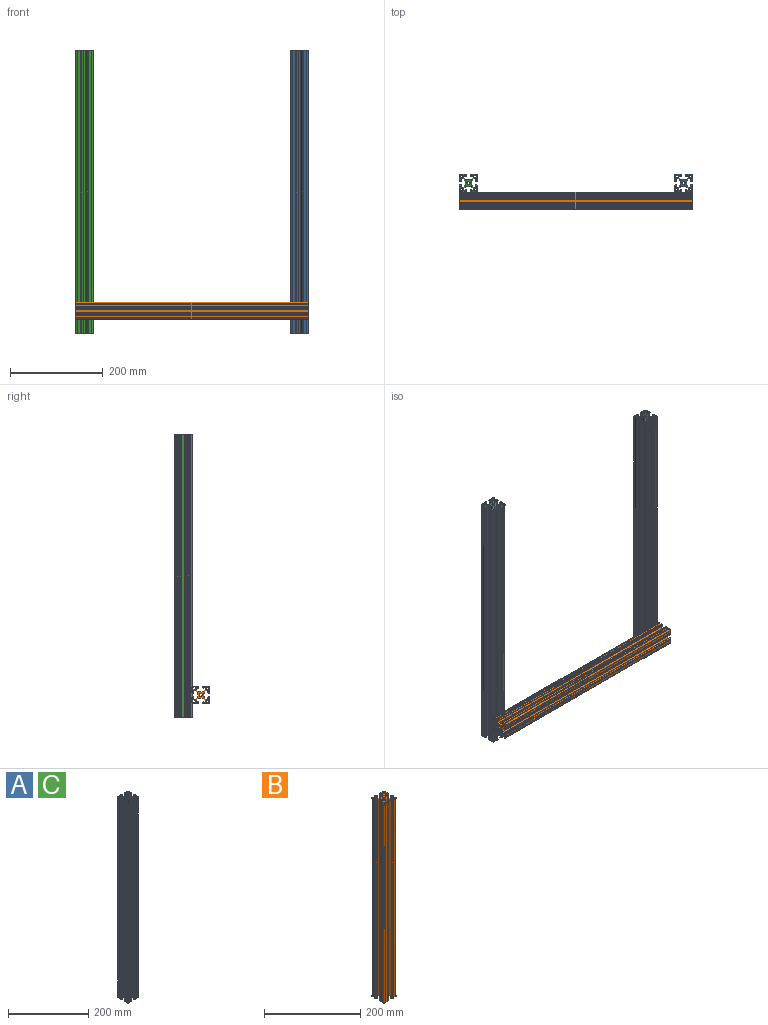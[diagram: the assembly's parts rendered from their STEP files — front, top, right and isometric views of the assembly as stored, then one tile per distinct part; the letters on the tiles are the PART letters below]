
ASSEMBLY  parts=3 mates=5
PART A: 171 faces, bbox 38.1x38.1x609.6 mm
  f0: cylinder r=4.75mm len=609.6mm, axis (0,0,-1), area 2273.9mm2, adj f1,f168,f169,f170
  f1: plane 609.6x4.01mm, normal (0.71,0.71,0), area 3452.7mm2, adj f0,f2,f169,f170
  f2: cylinder r=0.89mm len=609.6mm, axis (0,0,-1), area 425.5mm2, adj f1,f3,f169,f170
  f3: plane 609.6x1.77mm, normal (1,0,0), area 1081.7mm2, adj f2,f4,f169,f170
  f4: cylinder r=1.27mm len=609.6mm, axis (0,0,-1), area 1216.1mm2, adj f3,f5,f169,f170
  f5: plane 609.6x2.2mm, normal (0,-1,0), area 1342.9mm2, adj f4,f6,f169,f170
  f6: plane 609.6x0.84mm, normal (-1,0,0), area 511.3mm2, adj f5,f7,f169,f170
  f7: plane 609.6x1.18mm, normal (0,-1,0), area 716.5mm2, adj f6,f8,f169,f170
  f8: cylinder r=1.57mm len=609.6mm, axis (0,0,-1), area 1508mm2, adj f7,f9,f169,f170
  f9: plane 609.6x0.91mm, normal (1,0,0), area 557.4mm2, adj f8,f10,f169,f170
  f10: cylinder r=1.57mm len=609.6mm, axis (0,0,-1), area 1508mm2, adj f9,f11,f169,f170
  f11: plane 609.6x2.34mm, normal (0,1,0), area 1424.5mm2, adj f10,f12,f169,f170
  f12: cylinder r=0.76mm len=609.6mm, axis (0,0,-1), area 1459.3mm2, adj f11,f13,f169,f170
  f13: plane 609.6x4.83mm, normal (0,1,0), area 2941.9mm2, adj f12,f14,f169,f170
  f14: cylinder r=0.76mm len=609.6mm, axis (0,0,-1), area 1459.3mm2, adj f13,f15,f169,f170
  f15: plane 609.6x0.03mm, normal (0,1,0), area 15.5mm2, adj f14,f16,f169,f170
  f16: cylinder r=3.17mm len=609.6mm, axis (0,0,-1), area 3040.2mm2, adj f15,f17,f169,f170
  f17: plane 609.6x0.03mm, normal (-1,0,0), area 15.5mm2, adj f16,f18,f169,f170
  f18: cylinder r=0.76mm len=609.6mm, axis (0,0,-1), area 1459.3mm2, adj f17,f19,f169,f170
  f19: plane 609.6x4.83mm, normal (-1,0,0), area 2941.9mm2, adj f18,f20,f169,f170
  f20: cylinder r=0.76mm len=609.6mm, axis (0,0,-1), area 1459.3mm2, adj f19,f21,f169,f170
  f21: plane 609.6x2.34mm, normal (-1,0,0), area 1424.5mm2, adj f20,f22,f169,f170
  f22: cylinder r=1.57mm len=609.6mm, axis (0,0,-1), area 1508mm2, adj f21,f23,f169,f170
  f23: plane 609.6x0.91mm, normal (0,-1,0), area 557.4mm2, adj f22,f24,f169,f170
  f24: cylinder r=1.57mm len=609.6mm, axis (0,0,-1), area 1508mm2, adj f23,f25,f169,f170
  f25: plane 609.6x1.11mm, normal (1,0,0), area 677.8mm2, adj f24,f26,f169,f170
  f26: plane 609.6x0.89mm, normal (0,1,0), area 544.4mm2, adj f25,f27,f169,f170
  f27: plane 609.6x2.17mm, normal (1,0,0), area 1322mm2, adj f26,f28,f169,f170
  f28: cylinder r=1.27mm len=609.6mm, axis (0,0,-1), area 1216.1mm2, adj f27,f29,f169,f170
  f29: plane 609.6x1.87mm, normal (0,-1,0), area 1137.7mm2, adj f28,f30,f169,f170
  f30: cylinder r=0.89mm len=609.6mm, axis (0,0,-1), area 425.6mm2, adj f29,f31,f169,f170
  f31: plane 609.6x3.97mm, normal (-0.71,-0.71,0), area 3419.1mm2, adj f30,f32,f169,f170
  f32: cylinder r=4.75mm len=609.6mm, axis (0,0,-1), area 2274.3mm2, adj f31,f33,f169,f170
  f33: plane 609.6x5.21mm, normal (-1,0,0), area 3175.2mm2, adj f32,f34,f169,f170
  f34: cylinder r=4.75mm len=609.6mm, axis (0,0,-1), area 2274.3mm2, adj f33,f35,f169,f170
  f35: plane 609.6x3.97mm, normal (-0.71,0.71,0), area 3419.1mm2, adj f34,f36,f169,f170
  f36: cylinder r=0.89mm len=609.6mm, axis (0,0,-1), area 425.6mm2, adj f35,f37,f169,f170
  f37: plane 609.6x1.87mm, normal (0,1,0), area 1137.7mm2, adj f36,f38,f169,f170
  f38: cylinder r=1.27mm len=609.6mm, axis (0,0,-1), area 1216.1mm2, adj f37,f39,f169,f170
  f39: plane 609.6x2.17mm, normal (1,0,0), area 1322mm2, adj f38,f40,f169,f170
  f40: plane 609.6x0.89mm, normal (0,-1,0), area 544.4mm2, adj f39,f41,f169,f170
  f41: plane 609.6x1.11mm, normal (1,0,0), area 677.8mm2, adj f40,f42,f169,f170
  f42: cylinder r=1.57mm len=609.6mm, axis (0,0,-1), area 1508mm2, adj f41,f43,f169,f170
  f43: plane 609.6x0.91mm, normal (0,1,0), area 557.4mm2, adj f42,f44,f169,f170
  f44: cylinder r=1.57mm len=609.6mm, axis (0,0,-1), area 1508mm2, adj f43,f45,f169,f170
  f45: plane 609.6x2.34mm, normal (-1,0,0), area 1424.5mm2, adj f44,f46,f169,f170
  f46: cylinder r=0.76mm len=609.6mm, axis (0,0,-1), area 1459.3mm2, adj f45,f47,f169,f170
  f47: plane 609.6x4.83mm, normal (-1,0,0), area 2941.9mm2, adj f46,f48,f169,f170
  f48: cylinder r=0.76mm len=609.6mm, axis (0,0,-1), area 1459.3mm2, adj f47,f49,f169,f170
  f49: plane 609.6x0.03mm, normal (-1,0,0), area 15.5mm2, adj f48,f50,f169,f170
  f50: cylinder r=3.17mm len=609.6mm, axis (0,0,-1), area 3040.2mm2, adj f49,f51,f169,f170
  f51: plane 609.6x0.03mm, normal (0,-1,0), area 15.5mm2, adj f50,f52,f169,f170
  f52: cylinder r=0.76mm len=609.6mm, axis (0,0,-1), area 1459.3mm2, adj f51,f53,f169,f170
  f53: plane 609.6x4.83mm, normal (0,-1,0), area 2941.9mm2, adj f52,f54,f169,f170
  f54: cylinder r=0.76mm len=609.6mm, axis (0,0,-1), area 1459.3mm2, adj f53,f55,f169,f170
  f55: plane 609.6x2.34mm, normal (0,-1,0), area 1424.5mm2, adj f54,f56,f169,f170
  f56: cylinder r=1.57mm len=609.6mm, axis (0,0,-1), area 1508mm2, adj f55,f57,f169,f170
  f57: plane 609.6x0.91mm, normal (1,0,0), area 557.4mm2, adj f56,f58,f169,f170
  f58: cylinder r=1.57mm len=609.6mm, axis (0,0,-1), area 1508mm2, adj f57,f59,f169,f170
  f59: plane 609.6x1.18mm, normal (0,1,0), area 716.5mm2, adj f58,f60,f169,f170
  f60: plane 609.6x0.84mm, normal (-1,0,0), area 511.3mm2, adj f59,f61,f169,f170
  f61: plane 609.6x2.2mm, normal (0,1,0), area 1342.9mm2, adj f60,f62,f169,f170
  f62: cylinder r=1.27mm len=609.6mm, axis (0,0,-1), area 1216.1mm2, adj f61,f63,f169,f170
  f63: plane 609.6x1.77mm, normal (1,0,0), area 1081.7mm2, adj f62,f64,f169,f170
  f64: cylinder r=0.89mm len=609.6mm, axis (0,0,-1), area 425.5mm2, adj f63,f65,f169,f170
  f65: plane 609.6x4.01mm, normal (0.71,-0.71,0), area 3452.7mm2, adj f64,f66,f169,f170
  f66: cylinder r=4.75mm len=609.6mm, axis (0,0,-1), area 2273.9mm2, adj f65,f67,f169,f170
  f67: plane 609.6x5.33mm, normal (0,-1,0), area 3246.9mm2, adj f66,f68,f169,f170
  f68: cylinder r=4.75mm len=609.6mm, axis (0,0,-1), area 2273.9mm2, adj f67,f69,f169,f170
  f69: plane 609.6x4.01mm, normal (-0.71,-0.71,0), area 3452.7mm2, adj f68,f70,f169,f170
  f70: cylinder r=0.89mm len=609.6mm, axis (0,0,-1), area 425.5mm2, adj f69,f71,f169,f170
  f71: plane 609.6x1.77mm, normal (-1,0,0), area 1081.7mm2, adj f70,f72,f169,f170
  f72: cylinder r=1.27mm len=609.6mm, axis (0,0,-1), area 1216.1mm2, adj f71,f73,f169,f170
  f73: plane 609.6x2.2mm, normal (0,1,0), area 1342.9mm2, adj f72,f74,f169,f170
  f74: plane 609.6x0.84mm, normal (1,0,0), area 511.3mm2, adj f73,f75,f169,f170
  f75: plane 609.6x1.18mm, normal (0,1,0), area 716.5mm2, adj f74,f76,f169,f170
  f76: cylinder r=1.57mm len=609.6mm, axis (0,0,-1), area 1508mm2, adj f75,f77,f169,f170
  f77: plane 609.6x0.91mm, normal (-1,0,0), area 557.4mm2, adj f76,f78,f169,f170
  f78: cylinder r=1.57mm len=609.6mm, axis (0,0,-1), area 1508mm2, adj f77,f79,f169,f170
  f79: plane 609.6x2.34mm, normal (0,-1,0), area 1424.5mm2, adj f78,f80,f169,f170
  f80: cylinder r=0.76mm len=609.6mm, axis (0,0,-1), area 1459.3mm2, adj f79,f81,f169,f170
  f81: plane 609.6x4.83mm, normal (0,-1,0), area 2941.9mm2, adj f80,f82,f169,f170
  f82: cylinder r=0.76mm len=609.6mm, axis (0,0,-1), area 1459.3mm2, adj f81,f83,f169,f170
  f83: plane 609.6x0.03mm, normal (0,-1,0), area 15.5mm2, adj f82,f84,f169,f170
  f84: cylinder r=3.17mm len=609.6mm, axis (0,0,-1), area 3040.2mm2, adj f83,f85,f169,f170
  f85: plane 609.6x0.03mm, normal (1,0,0), area 15.5mm2, adj f84,f86,f169,f170
  f86: cylinder r=0.76mm len=609.6mm, axis (0,0,-1), area 1459.3mm2, adj f85,f87,f169,f170
  f87: plane 609.6x4.83mm, normal (1,0,0), area 2941.9mm2, adj f86,f88,f169,f170
  f88: cylinder r=0.76mm len=609.6mm, axis (0,0,-1), area 1459.3mm2, adj f87,f89,f169,f170
  f89: plane 609.6x2.34mm, normal (1,0,0), area 1424.5mm2, adj f88,f90,f169,f170
  f90: cylinder r=1.57mm len=609.6mm, axis (0,0,-1), area 1508mm2, adj f89,f91,f169,f170
  f91: plane 609.6x0.91mm, normal (0,1,0), area 557.4mm2, adj f90,f92,f169,f170
  f92: cylinder r=1.57mm len=609.6mm, axis (0,0,-1), area 1508mm2, adj f91,f93,f169,f170
  f93: plane 609.6x1.11mm, normal (-1,0,0), area 677.8mm2, adj f92,f94,f169,f170
  f94: plane 609.6x0.89mm, normal (0,-1,0), area 544.4mm2, adj f93,f95,f169,f170
  f95: plane 609.6x2.17mm, normal (-1,0,0), area 1322mm2, adj f94,f96,f169,f170
  f96: cylinder r=1.27mm len=609.6mm, axis (0,0,-1), area 1216.1mm2, adj f95,f97,f169,f170
  f97: plane 609.6x1.87mm, normal (0,1,0), area 1137.7mm2, adj f96,f98,f169,f170
  f98: cylinder r=0.89mm len=609.6mm, axis (0,0,-1), area 425.6mm2, adj f97,f99,f169,f170
  f99: plane 609.6x3.97mm, normal (0.71,0.71,0), area 3419.1mm2, adj f98,f100,f169,f170
  f100: cylinder r=4.75mm len=609.6mm, axis (0,0,-1), area 2274.3mm2, adj f99,f101,f169,f170
  f101: plane 609.6x5.21mm, normal (1,0,0), area 3175.2mm2, adj f100,f102,f169,f170
  f102: cylinder r=4.75mm len=609.6mm, axis (0,0,-1), area 2274.3mm2, adj f101,f103,f169,f170
  f103: plane 609.6x3.97mm, normal (0.71,-0.71,0), area 3419.1mm2, adj f102,f104,f169,f170
  f104: cylinder r=0.89mm len=609.6mm, axis (0,0,-1), area 425.6mm2, adj f103,f105,f169,f170
  f105: plane 609.6x1.87mm, normal (0,-1,0), area 1137.7mm2, adj f104,f106,f169,f170
  f106: cylinder r=1.27mm len=609.6mm, axis (0,0,-1), area 1216.1mm2, adj f105,f107,f169,f170
  f107: plane 609.6x2.17mm, normal (-1,0,0), area 1322mm2, adj f106,f108,f169,f170
  f108: plane 609.6x0.89mm, normal (0,1,0), area 544.4mm2, adj f107,f109,f169,f170
  f109: plane 609.6x1.11mm, normal (-1,0,0), area 677.8mm2, adj f108,f110,f169,f170
  f110: cylinder r=1.57mm len=609.6mm, axis (0,0,-1), area 1508mm2, adj f109,f111,f169,f170
  f111: plane 609.6x0.91mm, normal (0,-1,0), area 557.4mm2, adj f110,f112,f169,f170
  f112: cylinder r=1.57mm len=609.6mm, axis (0,0,-1), area 1508mm2, adj f111,f113,f169,f170
  f113: plane 609.6x2.34mm, normal (1,0,0), area 1424.5mm2, adj f112,f114,f169,f170
  f114: cylinder r=0.76mm len=609.6mm, axis (0,0,-1), area 1459.3mm2, adj f113,f115,f169,f170
  f115: plane 609.6x4.83mm, normal (1,0,0), area 2941.9mm2, adj f114,f116,f169,f170
  f116: cylinder r=0.76mm len=609.6mm, axis (0,0,-1), area 1459.3mm2, adj f115,f117,f169,f170
  f117: plane 609.6x0.03mm, normal (1,0,0), area 15.5mm2, adj f116,f118,f169,f170
  f118: cylinder r=3.17mm len=609.6mm, axis (0,0,-1), area 3040.2mm2, adj f117,f119,f169,f170
  f119: plane 609.6x0.03mm, normal (0,1,0), area 15.5mm2, adj f118,f120,f169,f170
  f120: cylinder r=0.76mm len=609.6mm, axis (0,0,-1), area 1459.3mm2, adj f119,f121,f169,f170
  f121: plane 609.6x4.83mm, normal (0,1,0), area 2941.9mm2, adj f120,f122,f169,f170
  f122: cylinder r=0.76mm len=609.6mm, axis (0,0,-1), area 1459.3mm2, adj f121,f123,f169,f170
  f123: plane 609.6x2.34mm, normal (0,1,0), area 1424.5mm2, adj f122,f124,f169,f170
  f124: cylinder r=1.57mm len=609.6mm, axis (0,0,-1), area 1508mm2, adj f123,f125,f169,f170
  f125: plane 609.6x0.91mm, normal (-1,0,0), area 557.4mm2, adj f124,f126,f169,f170
  f126: cylinder r=1.57mm len=609.6mm, axis (0,0,-1), area 1508mm2, adj f125,f127,f169,f170
  f127: plane 609.6x1.18mm, normal (0,-1,0), area 716.5mm2, adj f126,f128,f169,f170
  f128: plane 609.6x0.84mm, normal (1,0,0), area 511.3mm2, adj f127,f129,f169,f170
  f129: plane 609.6x2.2mm, normal (0,-1,0), area 1342.9mm2, adj f128,f130,f169,f170
  f130: cylinder r=1.27mm len=609.6mm, axis (0,0,-1), area 1216.1mm2, adj f129,f131,f169,f170
  f131: plane 609.6x1.77mm, normal (-1,0,0), area 1081.7mm2, adj f130,f132,f169,f170
  f132: cylinder r=0.89mm len=609.6mm, axis (0,0,-1), area 425.5mm2, adj f131,f133,f169,f170
  f133: plane 609.6x4.01mm, normal (-0.71,0.71,0), area 3452.7mm2, adj f132,f134,f169,f170
  f134: cylinder r=4.75mm len=609.6mm, axis (0,0,-1), area 2273.9mm2, adj f133,f168,f169,f170
  f135: cylinder r=0.38mm len=609.6mm, axis (0,0,-1), area 364.8mm2, adj f136,f163,f169,f170
  f136: plane 609.6x2.24mm, normal (1,0,0), area 1362.6mm2, adj f135,f137,f169,f170
  f137: cylinder r=2.79mm len=609.6mm, axis (0,0,-1), area 2675.4mm2, adj f136,f138,f169,f170
  f138: plane 609.6x2.24mm, normal (0,-1,0), area 1362.6mm2, adj f137,f139,f169,f170
  f139: cylinder r=0.38mm len=609.6mm, axis (0,0,-1), area 364.8mm2, adj f138,f140,f169,f170
  f140: plane 609.6x4.65mm, normal (-1,0,0), area 2833.5mm2, adj f139,f141,f169,f170
  f141: cylinder r=0.38mm len=609.6mm, axis (0,0,-1), area 364.8mm2, adj f140,f163,f169,f170
  f142: cylinder r=0.38mm len=609.6mm, axis (0,0,-1), area 364.8mm2, adj f143,f164,f169,f170
  f143: plane 609.6x4.65mm, normal (0,1,0), area 2833.5mm2, adj f142,f144,f169,f170
  f144: cylinder r=0.38mm len=609.6mm, axis (0,0,-1), area 364.8mm2, adj f143,f145,f169,f170
  f145: plane 609.6x4.65mm, normal (1,0,0), area 2833.5mm2, adj f144,f146,f169,f170
  f146: cylinder r=0.38mm len=609.6mm, axis (0,0,-1), area 364.8mm2, adj f145,f147,f169,f170
  f147: plane 609.6x2.24mm, normal (0,-1,0), area 1362.6mm2, adj f146,f148,f169,f170
  f148: cylinder r=2.79mm len=609.6mm, axis (0,0,-1), area 2675.4mm2, adj f147,f164,f169,f170
  f149: plane 609.6x2.24mm, normal (-1,0,0), area 1362.6mm2, adj f150,f165,f169,f170
  f150: cylinder r=2.79mm len=609.6mm, axis (0,0,-1), area 2675.4mm2, adj f149,f151,f169,f170
  f151: plane 609.6x2.24mm, normal (0,1,0), area 1362.6mm2, adj f150,f152,f169,f170
  f152: cylinder r=0.38mm len=609.6mm, axis (0,0,-1), area 364.8mm2, adj f151,f153,f169,f170
  f153: plane 609.6x4.65mm, normal (1,0,0), area 2833.5mm2, adj f152,f154,f169,f170
  f154: cylinder r=0.38mm len=609.6mm, axis (0,0,-1), area 364.8mm2, adj f153,f155,f169,f170
  f155: plane 609.6x4.65mm, normal (0,-1,0), area 2833.5mm2, adj f154,f165,f169,f170
  f156: plane 609.6x4.65mm, normal (-1,0,0), area 2833.5mm2, adj f157,f166,f169,f170
  f157: cylinder r=0.38mm len=609.6mm, axis (0,0,-1), area 364.8mm2, adj f156,f158,f169,f170
  f158: plane 609.6x2.24mm, normal (0,1,0), area 1362.6mm2, adj f157,f159,f169,f170
  f159: cylinder r=2.79mm len=609.6mm, axis (0,0,-1), area 2675.4mm2, adj f158,f160,f169,f170
  f160: plane 609.6x2.24mm, normal (1,0,0), area 1362.6mm2, adj f159,f161,f169,f170
  f161: cylinder r=0.38mm len=609.6mm, axis (0,0,-1), area 364.8mm2, adj f160,f162,f169,f170
  f162: plane 609.6x4.65mm, normal (0,-1,0), area 2833.5mm2, adj f161,f166,f169,f170
  f163: plane 609.6x4.65mm, normal (0,1,0), area 2833.5mm2, adj f135,f141,f169,f170
  f164: plane 609.6x2.24mm, normal (-1,0,0), area 1362.6mm2, adj f142,f148,f169,f170
  f165: cylinder r=0.38mm len=609.6mm, axis (0,0,-1), area 364.8mm2, adj f149,f155,f169,f170
  f166: cylinder r=0.38mm len=609.6mm, axis (0,0,-1), area 364.8mm2, adj f156,f162,f169,f170
  f167: cylinder r=3.33mm len=609.6mm, axis (0,0,-1), area 12744.7mm2, adj f169,f170
  f168: plane 609.6x5.33mm, normal (0,1,0), area 3246.9mm2, adj f0,f134,f169,f170
  f169: plane 38.1x38.1mm, normal (0,0,1), area 578.8mm2, adj f0,f1,f2,f3,f4,f5,f6,f7
  f170: plane 38.1x38.1mm, normal (0,0,-1), area 578.8mm2, adj f0,f1,f2,f3,f4,f5,f6,f7
PART B: 171 faces, bbox 38.1x38.1x502.4 mm
  f0: cylinder r=4.75mm len=502.41mm, axis (0,0,-1), area 1874mm2, adj f1,f168,f169,f170
  f1: plane 502.41x4.01mm, normal (0.71,0.71,0), area 2845.6mm2, adj f0,f2,f169,f170
  f2: cylinder r=0.89mm len=502.41mm, axis (0,0,-1), area 350.6mm2, adj f1,f3,f169,f170
  f3: plane 502.41x1.77mm, normal (1,0,0), area 891.5mm2, adj f2,f4,f169,f170
  f4: cylinder r=1.27mm len=502.41mm, axis (0,0,-1), area 1002.3mm2, adj f3,f5,f169,f170
  f5: plane 502.41x2.2mm, normal (0,-1,0), area 1106.7mm2, adj f4,f6,f169,f170
  f6: plane 502.41x0.84mm, normal (-1,0,0), area 421.4mm2, adj f5,f7,f169,f170
  f7: plane 502.41x1.18mm, normal (0,-1,0), area 590.5mm2, adj f6,f8,f169,f170
  f8: cylinder r=1.57mm len=502.41mm, axis (0,0,-1), area 1242.8mm2, adj f7,f9,f169,f170
  f9: plane 502.41x0.91mm, normal (1,0,0), area 459.4mm2, adj f8,f10,f169,f170
  f10: cylinder r=1.57mm len=502.41mm, axis (0,0,-1), area 1242.8mm2, adj f9,f11,f169,f170
  f11: plane 502.41x2.34mm, normal (0,1,0), area 1174mm2, adj f10,f12,f169,f170
  f12: cylinder r=0.76mm len=502.41mm, axis (0,0,-1), area 1202.7mm2, adj f11,f13,f169,f170
  f13: plane 502.41x4.83mm, normal (0,1,0), area 2424.6mm2, adj f12,f14,f169,f170
  f14: cylinder r=0.76mm len=502.41mm, axis (0,0,-1), area 1202.7mm2, adj f13,f15,f169,f170
  f15: plane 502.41x0.03mm, normal (0,1,0), area 12.8mm2, adj f14,f16,f169,f170
  f16: cylinder r=3.17mm len=502.41mm, axis (0,0,-1), area 2505.7mm2, adj f15,f17,f169,f170
  f17: plane 502.41x0.03mm, normal (-1,0,0), area 12.8mm2, adj f16,f18,f169,f170
  f18: cylinder r=0.76mm len=502.41mm, axis (0,0,-1), area 1202.7mm2, adj f17,f19,f169,f170
  f19: plane 502.41x4.83mm, normal (-1,0,0), area 2424.6mm2, adj f18,f20,f169,f170
  f20: cylinder r=0.76mm len=502.41mm, axis (0,0,-1), area 1202.7mm2, adj f19,f21,f169,f170
  f21: plane 502.41x2.34mm, normal (-1,0,0), area 1174mm2, adj f20,f22,f169,f170
  f22: cylinder r=1.57mm len=502.41mm, axis (0,0,-1), area 1242.8mm2, adj f21,f23,f169,f170
  f23: plane 502.41x0.91mm, normal (0,-1,0), area 459.4mm2, adj f22,f24,f169,f170
  f24: cylinder r=1.57mm len=502.41mm, axis (0,0,-1), area 1242.8mm2, adj f23,f25,f169,f170
  f25: plane 502.41x1.11mm, normal (1,0,0), area 558.6mm2, adj f24,f26,f169,f170
  f26: plane 502.41x0.89mm, normal (0,1,0), area 448.7mm2, adj f25,f27,f169,f170
  f27: plane 502.41x2.17mm, normal (1,0,0), area 1089.5mm2, adj f26,f28,f169,f170
  f28: cylinder r=1.27mm len=502.41mm, axis (0,0,-1), area 1002.3mm2, adj f27,f29,f169,f170
  f29: plane 502.41x1.87mm, normal (0,-1,0), area 937.6mm2, adj f28,f30,f169,f170
  f30: cylinder r=0.89mm len=502.41mm, axis (0,0,-1), area 350.8mm2, adj f29,f31,f169,f170
  f31: plane 502.41x3.97mm, normal (-0.71,-0.71,0), area 2817.9mm2, adj f30,f32,f169,f170
  f32: cylinder r=4.75mm len=502.41mm, axis (0,0,-1), area 1874.4mm2, adj f31,f33,f169,f170
  f33: plane 502.41x5.21mm, normal (-1,0,0), area 2616.9mm2, adj f32,f34,f169,f170
  f34: cylinder r=4.75mm len=502.41mm, axis (0,0,-1), area 1874.4mm2, adj f33,f35,f169,f170
  f35: plane 502.41x3.97mm, normal (-0.71,0.71,0), area 2817.9mm2, adj f34,f36,f169,f170
  f36: cylinder r=0.89mm len=502.41mm, axis (0,0,-1), area 350.8mm2, adj f35,f37,f169,f170
  f37: plane 502.41x1.87mm, normal (0,1,0), area 937.6mm2, adj f36,f38,f169,f170
  f38: cylinder r=1.27mm len=502.41mm, axis (0,0,-1), area 1002.3mm2, adj f37,f39,f169,f170
  f39: plane 502.41x2.17mm, normal (1,0,0), area 1089.5mm2, adj f38,f40,f169,f170
  f40: plane 502.41x0.89mm, normal (0,-1,0), area 448.7mm2, adj f39,f41,f169,f170
  f41: plane 502.41x1.11mm, normal (1,0,0), area 558.6mm2, adj f40,f42,f169,f170
  f42: cylinder r=1.57mm len=502.41mm, axis (0,0,-1), area 1242.8mm2, adj f41,f43,f169,f170
  f43: plane 502.41x0.91mm, normal (0,1,0), area 459.4mm2, adj f42,f44,f169,f170
  f44: cylinder r=1.57mm len=502.41mm, axis (0,0,-1), area 1242.8mm2, adj f43,f45,f169,f170
  f45: plane 502.41x2.34mm, normal (-1,0,0), area 1174mm2, adj f44,f46,f169,f170
  f46: cylinder r=0.76mm len=502.41mm, axis (0,0,-1), area 1202.7mm2, adj f45,f47,f169,f170
  f47: plane 502.41x4.83mm, normal (-1,0,0), area 2424.6mm2, adj f46,f48,f169,f170
  f48: cylinder r=0.76mm len=502.41mm, axis (0,0,-1), area 1202.7mm2, adj f47,f49,f169,f170
  f49: plane 502.41x0.03mm, normal (-1,0,0), area 12.8mm2, adj f48,f50,f169,f170
  f50: cylinder r=3.17mm len=502.41mm, axis (0,0,-1), area 2505.7mm2, adj f49,f51,f169,f170
  f51: plane 502.41x0.03mm, normal (0,-1,0), area 12.8mm2, adj f50,f52,f169,f170
  f52: cylinder r=0.76mm len=502.41mm, axis (0,0,-1), area 1202.7mm2, adj f51,f53,f169,f170
  f53: plane 502.41x4.83mm, normal (0,-1,0), area 2424.6mm2, adj f52,f54,f169,f170
  f54: cylinder r=0.76mm len=502.41mm, axis (0,0,-1), area 1202.7mm2, adj f53,f55,f169,f170
  f55: plane 502.41x2.34mm, normal (0,-1,0), area 1174mm2, adj f54,f56,f169,f170
  f56: cylinder r=1.57mm len=502.41mm, axis (0,0,-1), area 1242.8mm2, adj f55,f57,f169,f170
  f57: plane 502.41x0.91mm, normal (1,0,0), area 459.4mm2, adj f56,f58,f169,f170
  f58: cylinder r=1.57mm len=502.41mm, axis (0,0,-1), area 1242.8mm2, adj f57,f59,f169,f170
  f59: plane 502.41x1.18mm, normal (0,1,0), area 590.5mm2, adj f58,f60,f169,f170
  f60: plane 502.41x0.84mm, normal (-1,0,0), area 421.4mm2, adj f59,f61,f169,f170
  f61: plane 502.41x2.2mm, normal (0,1,0), area 1106.7mm2, adj f60,f62,f169,f170
  f62: cylinder r=1.27mm len=502.41mm, axis (0,0,-1), area 1002.3mm2, adj f61,f63,f169,f170
  f63: plane 502.41x1.77mm, normal (1,0,0), area 891.5mm2, adj f62,f64,f169,f170
  f64: cylinder r=0.89mm len=502.41mm, axis (0,0,-1), area 350.6mm2, adj f63,f65,f169,f170
  f65: plane 502.41x4.01mm, normal (0.71,-0.71,0), area 2845.6mm2, adj f64,f66,f169,f170
  f66: cylinder r=4.75mm len=502.41mm, axis (0,0,-1), area 1874mm2, adj f65,f67,f169,f170
  f67: plane 502.41x5.33mm, normal (0,-1,0), area 2676mm2, adj f66,f68,f169,f170
  f68: cylinder r=4.75mm len=502.41mm, axis (0,0,-1), area 1874mm2, adj f67,f69,f169,f170
  f69: plane 502.41x4.01mm, normal (-0.71,-0.71,0), area 2845.6mm2, adj f68,f70,f169,f170
  f70: cylinder r=0.89mm len=502.41mm, axis (0,0,-1), area 350.6mm2, adj f69,f71,f169,f170
  f71: plane 502.41x1.77mm, normal (-1,0,0), area 891.5mm2, adj f70,f72,f169,f170
  f72: cylinder r=1.27mm len=502.41mm, axis (0,0,-1), area 1002.3mm2, adj f71,f73,f169,f170
  f73: plane 502.41x2.2mm, normal (0,1,0), area 1106.7mm2, adj f72,f74,f169,f170
  f74: plane 502.41x0.84mm, normal (1,0,0), area 421.4mm2, adj f73,f75,f169,f170
  f75: plane 502.41x1.18mm, normal (0,1,0), area 590.5mm2, adj f74,f76,f169,f170
  f76: cylinder r=1.57mm len=502.41mm, axis (0,0,-1), area 1242.8mm2, adj f75,f77,f169,f170
  f77: plane 502.41x0.91mm, normal (-1,0,0), area 459.4mm2, adj f76,f78,f169,f170
  f78: cylinder r=1.57mm len=502.41mm, axis (0,0,-1), area 1242.8mm2, adj f77,f79,f169,f170
  f79: plane 502.41x2.34mm, normal (0,-1,0), area 1174mm2, adj f78,f80,f169,f170
  f80: cylinder r=0.76mm len=502.41mm, axis (0,0,-1), area 1202.7mm2, adj f79,f81,f169,f170
  f81: plane 502.41x4.83mm, normal (0,-1,0), area 2424.6mm2, adj f80,f82,f169,f170
  f82: cylinder r=0.76mm len=502.41mm, axis (0,0,-1), area 1202.7mm2, adj f81,f83,f169,f170
  f83: plane 502.41x0.03mm, normal (0,-1,0), area 12.8mm2, adj f82,f84,f169,f170
  f84: cylinder r=3.17mm len=502.41mm, axis (0,0,-1), area 2505.7mm2, adj f83,f85,f169,f170
  f85: plane 502.41x0.03mm, normal (1,0,0), area 12.8mm2, adj f84,f86,f169,f170
  f86: cylinder r=0.76mm len=502.41mm, axis (0,0,-1), area 1202.7mm2, adj f85,f87,f169,f170
  f87: plane 502.41x4.83mm, normal (1,0,0), area 2424.6mm2, adj f86,f88,f169,f170
  f88: cylinder r=0.76mm len=502.41mm, axis (0,0,-1), area 1202.7mm2, adj f87,f89,f169,f170
  f89: plane 502.41x2.34mm, normal (1,0,0), area 1174mm2, adj f88,f90,f169,f170
  f90: cylinder r=1.57mm len=502.41mm, axis (0,0,-1), area 1242.8mm2, adj f89,f91,f169,f170
  f91: plane 502.41x0.91mm, normal (0,1,0), area 459.4mm2, adj f90,f92,f169,f170
  f92: cylinder r=1.57mm len=502.41mm, axis (0,0,-1), area 1242.8mm2, adj f91,f93,f169,f170
  f93: plane 502.41x1.11mm, normal (-1,0,0), area 558.6mm2, adj f92,f94,f169,f170
  f94: plane 502.41x0.89mm, normal (0,-1,0), area 448.7mm2, adj f93,f95,f169,f170
  f95: plane 502.41x2.17mm, normal (-1,0,0), area 1089.5mm2, adj f94,f96,f169,f170
  f96: cylinder r=1.27mm len=502.41mm, axis (0,0,-1), area 1002.3mm2, adj f95,f97,f169,f170
  f97: plane 502.41x1.87mm, normal (0,1,0), area 937.6mm2, adj f96,f98,f169,f170
  f98: cylinder r=0.89mm len=502.41mm, axis (0,0,-1), area 350.8mm2, adj f97,f99,f169,f170
  f99: plane 502.41x3.97mm, normal (0.71,0.71,0), area 2817.9mm2, adj f98,f100,f169,f170
  f100: cylinder r=4.75mm len=502.41mm, axis (0,0,-1), area 1874.4mm2, adj f99,f101,f169,f170
  f101: plane 502.41x5.21mm, normal (1,0,0), area 2616.9mm2, adj f100,f102,f169,f170
  f102: cylinder r=4.75mm len=502.41mm, axis (0,0,-1), area 1874.4mm2, adj f101,f103,f169,f170
  f103: plane 502.41x3.97mm, normal (0.71,-0.71,0), area 2817.9mm2, adj f102,f104,f169,f170
  f104: cylinder r=0.89mm len=502.41mm, axis (0,0,-1), area 350.8mm2, adj f103,f105,f169,f170
  f105: plane 502.41x1.87mm, normal (0,-1,0), area 937.6mm2, adj f104,f106,f169,f170
  f106: cylinder r=1.27mm len=502.41mm, axis (0,0,-1), area 1002.3mm2, adj f105,f107,f169,f170
  f107: plane 502.41x2.17mm, normal (-1,0,0), area 1089.5mm2, adj f106,f108,f169,f170
  f108: plane 502.41x0.89mm, normal (0,1,0), area 448.7mm2, adj f107,f109,f169,f170
  f109: plane 502.41x1.11mm, normal (-1,0,0), area 558.6mm2, adj f108,f110,f169,f170
  f110: cylinder r=1.57mm len=502.41mm, axis (0,0,-1), area 1242.8mm2, adj f109,f111,f169,f170
  f111: plane 502.41x0.91mm, normal (0,-1,0), area 459.4mm2, adj f110,f112,f169,f170
  f112: cylinder r=1.57mm len=502.41mm, axis (0,0,-1), area 1242.8mm2, adj f111,f113,f169,f170
  f113: plane 502.41x2.34mm, normal (1,0,0), area 1174mm2, adj f112,f114,f169,f170
  f114: cylinder r=0.76mm len=502.41mm, axis (0,0,-1), area 1202.7mm2, adj f113,f115,f169,f170
  f115: plane 502.41x4.83mm, normal (1,0,0), area 2424.6mm2, adj f114,f116,f169,f170
  f116: cylinder r=0.76mm len=502.41mm, axis (0,0,-1), area 1202.7mm2, adj f115,f117,f169,f170
  f117: plane 502.41x0.03mm, normal (1,0,0), area 12.8mm2, adj f116,f118,f169,f170
  f118: cylinder r=3.17mm len=502.41mm, axis (0,0,-1), area 2505.7mm2, adj f117,f119,f169,f170
  f119: plane 502.41x0.03mm, normal (0,1,0), area 12.8mm2, adj f118,f120,f169,f170
  f120: cylinder r=0.76mm len=502.41mm, axis (0,0,-1), area 1202.7mm2, adj f119,f121,f169,f170
  f121: plane 502.41x4.83mm, normal (0,1,0), area 2424.6mm2, adj f120,f122,f169,f170
  f122: cylinder r=0.76mm len=502.41mm, axis (0,0,-1), area 1202.7mm2, adj f121,f123,f169,f170
  f123: plane 502.41x2.34mm, normal (0,1,0), area 1174mm2, adj f122,f124,f169,f170
  f124: cylinder r=1.57mm len=502.41mm, axis (0,0,-1), area 1242.8mm2, adj f123,f125,f169,f170
  f125: plane 502.41x0.91mm, normal (-1,0,0), area 459.4mm2, adj f124,f126,f169,f170
  f126: cylinder r=1.57mm len=502.41mm, axis (0,0,-1), area 1242.8mm2, adj f125,f127,f169,f170
  f127: plane 502.41x1.18mm, normal (0,-1,0), area 590.5mm2, adj f126,f128,f169,f170
  f128: plane 502.41x0.84mm, normal (1,0,0), area 421.4mm2, adj f127,f129,f169,f170
  f129: plane 502.41x2.2mm, normal (0,-1,0), area 1106.7mm2, adj f128,f130,f169,f170
  f130: cylinder r=1.27mm len=502.41mm, axis (0,0,-1), area 1002.3mm2, adj f129,f131,f169,f170
  f131: plane 502.41x1.77mm, normal (-1,0,0), area 891.5mm2, adj f130,f132,f169,f170
  f132: cylinder r=0.89mm len=502.41mm, axis (0,0,-1), area 350.6mm2, adj f131,f133,f169,f170
  f133: plane 502.41x4.01mm, normal (-0.71,0.71,0), area 2845.6mm2, adj f132,f134,f169,f170
  f134: cylinder r=4.75mm len=502.41mm, axis (0,0,-1), area 1874mm2, adj f133,f168,f169,f170
  f135: cylinder r=0.38mm len=502.41mm, axis (0,0,-1), area 300.7mm2, adj f136,f163,f169,f170
  f136: plane 502.41x2.24mm, normal (1,0,0), area 1123mm2, adj f135,f137,f169,f170
  f137: cylinder r=2.79mm len=502.41mm, axis (0,0,-1), area 2205mm2, adj f136,f138,f169,f170
  f138: plane 502.41x2.24mm, normal (0,-1,0), area 1123mm2, adj f137,f139,f169,f170
  f139: cylinder r=0.38mm len=502.41mm, axis (0,0,-1), area 300.7mm2, adj f138,f140,f169,f170
  f140: plane 502.41x4.65mm, normal (-1,0,0), area 2335.3mm2, adj f139,f141,f169,f170
  f141: cylinder r=0.38mm len=502.41mm, axis (0,0,-1), area 300.7mm2, adj f140,f163,f169,f170
  f142: cylinder r=0.38mm len=502.41mm, axis (0,0,-1), area 300.7mm2, adj f143,f164,f169,f170
  f143: plane 502.41x4.65mm, normal (0,1,0), area 2335.3mm2, adj f142,f144,f169,f170
  f144: cylinder r=0.38mm len=502.41mm, axis (0,0,-1), area 300.7mm2, adj f143,f145,f169,f170
  f145: plane 502.41x4.65mm, normal (1,0,0), area 2335.3mm2, adj f144,f146,f169,f170
  f146: cylinder r=0.38mm len=502.41mm, axis (0,0,-1), area 300.7mm2, adj f145,f147,f169,f170
  f147: plane 502.41x2.24mm, normal (0,-1,0), area 1123mm2, adj f146,f148,f169,f170
  f148: cylinder r=2.79mm len=502.41mm, axis (0,0,-1), area 2205mm2, adj f147,f164,f169,f170
  f149: plane 502.41x2.24mm, normal (-1,0,0), area 1123mm2, adj f150,f165,f169,f170
  f150: cylinder r=2.79mm len=502.41mm, axis (0,0,-1), area 2205mm2, adj f149,f151,f169,f170
  f151: plane 502.41x2.24mm, normal (0,1,0), area 1123mm2, adj f150,f152,f169,f170
  f152: cylinder r=0.38mm len=502.41mm, axis (0,0,-1), area 300.7mm2, adj f151,f153,f169,f170
  f153: plane 502.41x4.65mm, normal (1,0,0), area 2335.3mm2, adj f152,f154,f169,f170
  f154: cylinder r=0.38mm len=502.41mm, axis (0,0,-1), area 300.7mm2, adj f153,f155,f169,f170
  f155: plane 502.41x4.65mm, normal (0,-1,0), area 2335.3mm2, adj f154,f165,f169,f170
  f156: plane 502.41x4.65mm, normal (-1,0,0), area 2335.3mm2, adj f157,f166,f169,f170
  f157: cylinder r=0.38mm len=502.41mm, axis (0,0,-1), area 300.7mm2, adj f156,f158,f169,f170
  f158: plane 502.41x2.24mm, normal (0,1,0), area 1123mm2, adj f157,f159,f169,f170
  f159: cylinder r=2.79mm len=502.41mm, axis (0,0,-1), area 2205mm2, adj f158,f160,f169,f170
  f160: plane 502.41x2.24mm, normal (1,0,0), area 1123mm2, adj f159,f161,f169,f170
  f161: cylinder r=0.38mm len=502.41mm, axis (0,0,-1), area 300.7mm2, adj f160,f162,f169,f170
  f162: plane 502.41x4.65mm, normal (0,-1,0), area 2335.3mm2, adj f161,f166,f169,f170
  f163: plane 502.41x4.65mm, normal (0,1,0), area 2335.3mm2, adj f135,f141,f169,f170
  f164: plane 502.41x2.24mm, normal (-1,0,0), area 1123mm2, adj f142,f148,f169,f170
  f165: cylinder r=0.38mm len=502.41mm, axis (0,0,-1), area 300.7mm2, adj f149,f155,f169,f170
  f166: cylinder r=0.38mm len=502.41mm, axis (0,0,-1), area 300.7mm2, adj f156,f162,f169,f170
  f167: cylinder r=3.33mm len=502.41mm, axis (0,0,-1), area 10503.8mm2, adj f169,f170
  f168: plane 502.41x5.33mm, normal (0,1,0), area 2676mm2, adj f0,f134,f169,f170
  f169: plane 38.1x38.1mm, normal (0,0,1), area 578.8mm2, adj f0,f1,f2,f3,f4,f5,f6,f7
  f170: plane 38.1x38.1mm, normal (0,0,-1), area 578.8mm2, adj f0,f1,f2,f3,f4,f5,f6,f7
PART C: same geometry as A
PLACE A t=(757.05,-99.89,215.63)mm
PLACE B rot(axis=(0,1,0),90deg) t=(432.45,-130.43,-41.25)mm
PLACE C t=(292.73,-99.89,215.63)mm
MATE planar C.f81 <-> B.f121  axis (0,-1,0) through (212.2,-111.38,215.63)mm
MATE planar B.f170 <-> C.f47  axis (-1,0,0) through (181.24,-127.83,-48.01)mm
MATE planar B.f167 <-> A.f87  axis (1,0,0) through (683.65,-130.43,-41.25)mm
MATE planar C.f170 <-> A.f170  axis (0,0,-1) through (202.96,-99.09,-89.17)mm
MATE planar C.f53 <-> A.f81  axis (0,-1,0) through (190.79,-111.38,-89.17)mm
